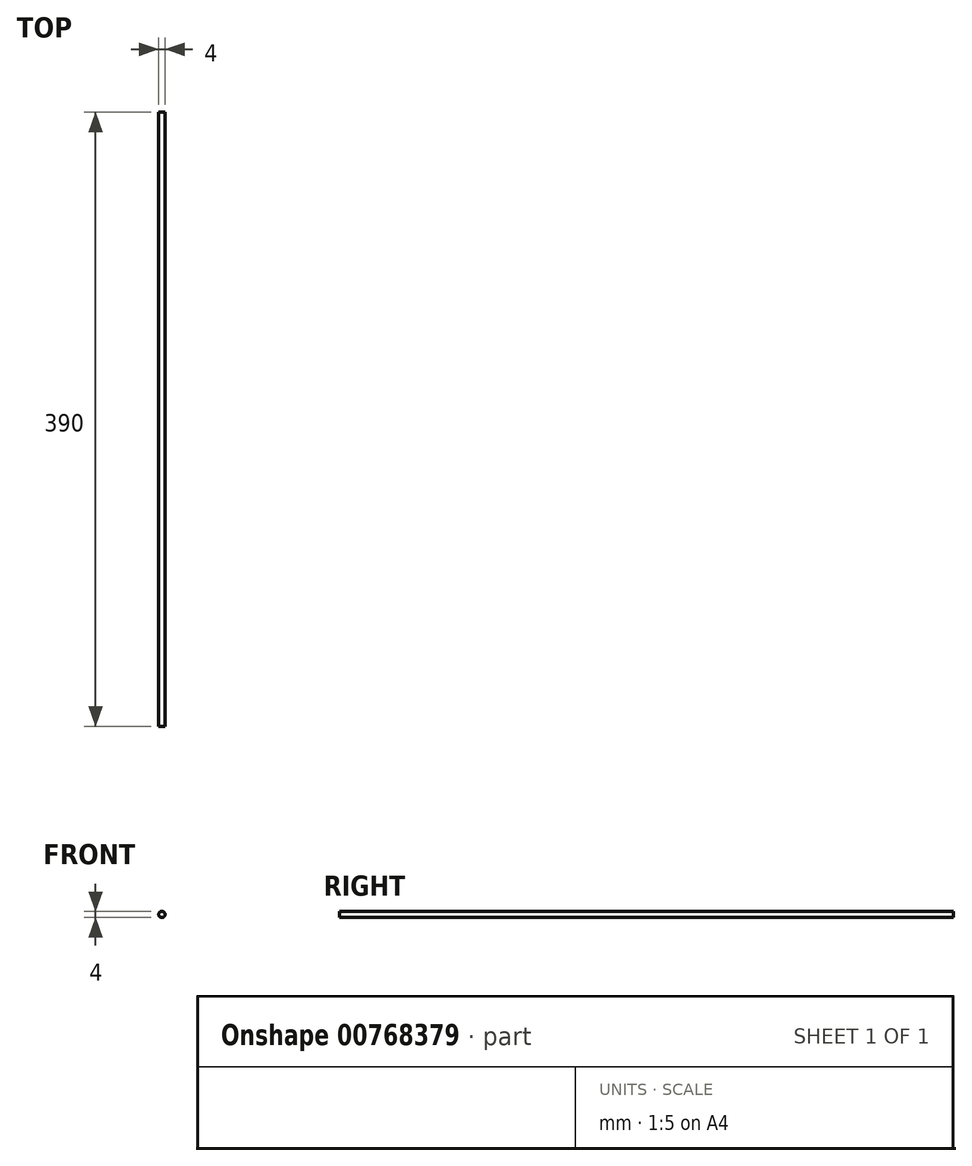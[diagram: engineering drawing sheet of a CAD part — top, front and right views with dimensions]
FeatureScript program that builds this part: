
annotation { "Feature Type Name" : "Feature", "Feature Type Description" : "" }
export const myFeature = defineFeature(function(context is Context, id is Id, definition is map)
    precondition{}
    {
        {
            var Q0;
            Q0=qCreatedBy(makeId("Front.planeOp"),FACE);
            var sketch = newSketch(context, id + "F0", { "sketchPlane" : qUnion([Q0])});
            skCircle(sketch, "E0", {"center": v(0, 0) * mm, "radius": 2 * mm});
            skSolve(sketch);
        }
        {
            var Q0;
            Q0=makeQuery(id+"F0.imprint","IMPRINT",FACE,{"disambiguationData":[TD([[makeQuery(id+"F0.imprint","IMPRINT",EDGE,{"derivedFrom":sQuery(id+"F0.wireOp",EDGE,"E0")}),1.0]])]});
            extrude(context, id + "F1", {"entities" : qUnion([Q0]), "depth" : 390 * mm, "offsetDistance" : 25 * mm});
        }
    });
